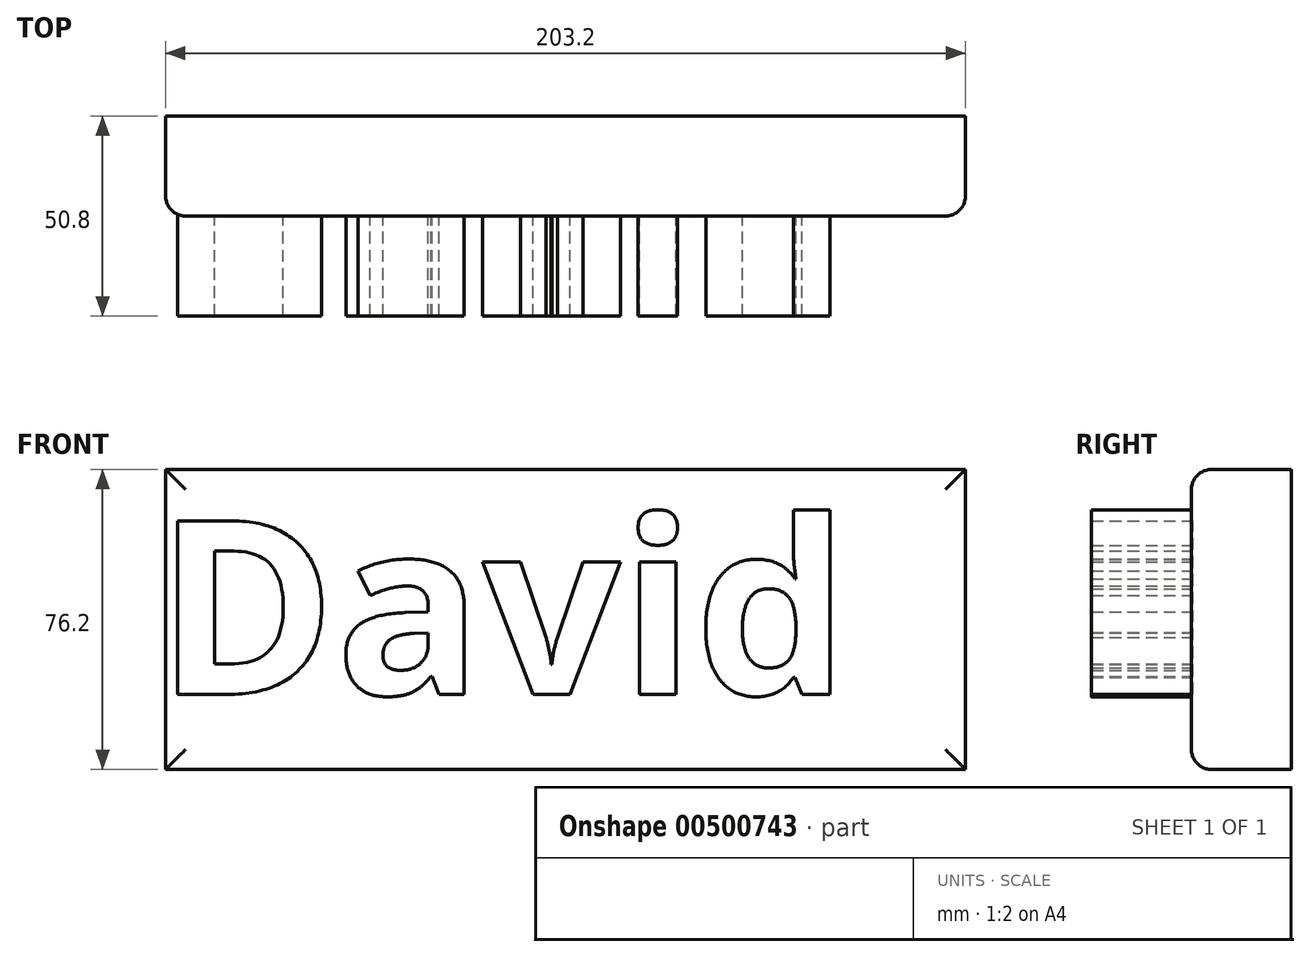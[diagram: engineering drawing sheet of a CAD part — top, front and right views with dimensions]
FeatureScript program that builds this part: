
annotation { "Feature Type Name" : "Feature", "Feature Type Description" : "" }
export const myFeature = defineFeature(function(context is Context, id is Id, definition is map)
    precondition{}
    {
        {
            var Q0;
            Q0=qCreatedBy(makeId("Front.planeOp"),FACE);
            var sketch = newSketch(context, id + "F0", { "sketchPlane" : qUnion([Q0])});
            skLineSegment(sketch, "E0.bottom", {"start": v(-109.5, 41.91) * mm, "end": v(93.7, 41.91) * mm});
            skLineSegment(sketch, "E0.top", {"start": v(-109.5, -34.29) * mm, "end": v(93.7, -34.29) * mm});
            skLineSegment(sketch, "E0.left", {"start": v(-109.5, 41.91) * mm, "end": v(-109.5, -34.29) * mm});
            skLineSegment(sketch, "E0.right", {"start": v(93.7, 41.91) * mm, "end": v(93.7, -34.29) * mm});
            skSolve(sketch);
        }
        {
            var Q0;
            Q0=makeQuery(id+"F0.imprint","IMPRINT",FACE,{"disambiguationData":[TD([[makeQuery(id+"F0.imprint","IMPRINT",EDGE,{"derivedFrom":sQuery(id+"F0.wireOp",EDGE,"E0.bottom")}),-1.0]])]});
            extrude(context, id + "F1", {"entities" : qUnion([Q0]), "depth" : 25.4 * mm});
        }
        {
            var Q0;
            Q0=makeQuery(id+"F1.opExtrude","CAP_FACE",FACE,{"disambiguationData":[OSD([sQuery(id+"F0.wireOp",EDGE,"E0.bottom"),sQuery(id+"F0.wireOp",EDGE,"E0.top"),sQuery(id+"F0.wireOp",EDGE,"E0.left"),sQuery(id+"F0.wireOp",EDGE,"E0.right")])],"isStart":false});
            fillet(context, id + "F2", {"entities" : qUnion([Q0]), "radius" : 5.08 * mm, "tangentPropagation" : true, "allowEdgeOverflow" : false});
        }
        {
            var Q0;
            Q0=qCreatedBy(makeId("Front.planeOp"),FACE);
            var sketch = newSketch(context, id + "F3", { "sketchPlane" : qUnion([Q0])});
            skText(sketch, "E1", { "text": "David ", "fontName": "OpenSans-Bold.ttf"});
            const initialGuessF3  = {"E1": [-0.11202, -0.01524, 1, 0, 0.04445]};
            skSetInitialGuess(sketch, initialGuessF3);
            skSolve(sketch);
        }
        {
            var Q0;
            Q0 = qSketchRegion(id + "F3", true);
            extrude(context, id + "F4", {"entities" : qUnion([Q0]), "operationType" : NewBodyOperationType.ADD, "depth" : 50.8 * mm});
        }
    });
